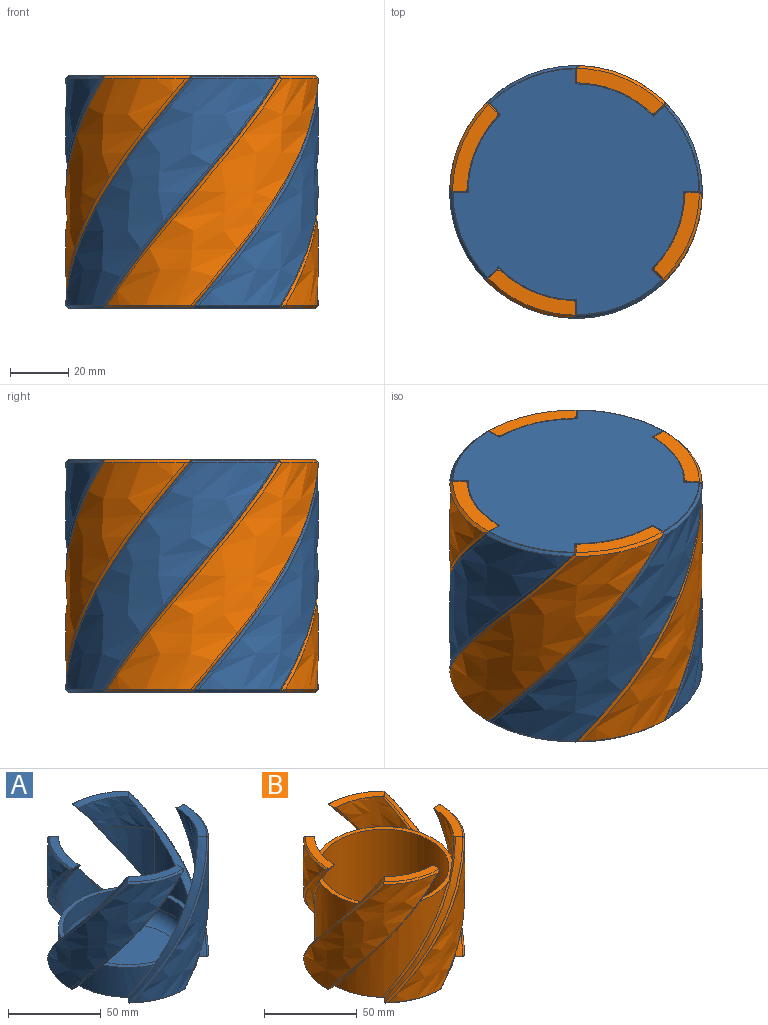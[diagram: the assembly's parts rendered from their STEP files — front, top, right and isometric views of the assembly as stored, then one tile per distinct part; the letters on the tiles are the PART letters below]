
ASSEMBLY  parts=2 mates=1
PART A: 76 faces, bbox 90.4x90.4x84.8 mm
  f0: cylinder r=35mm len=70mm, axis (0,0,-1), area 2199.1mm2, adj f10,f75
  f1: plane 55x55mm, normal (0,0,1), area 2375.8mm2, adj f75
  f2: extruded ~40x21.23mm, area 633.3mm2, adj f9,f10,f35,f62
  f3: extruded ~40x20.3mm, area 589.1mm2, adj f6,f29,f34
  f4: extruded ~40x21.23mm, area 636.5mm2, adj f7,f10,f30,f60
  f5: extruded ~51.58x28.32mm, area 652mm2, adj f8,f10,f22,f26,f61
  f6: cylinder r=37.5mm len=40mm, axis (0,0,1), area 589mm2, adj f3,f10,f31
  f7: cylinder r=37.5mm len=40mm, axis (0,0,1), area 589mm2, adj f4,f10,f27
  f8: cylinder r=37.5mm len=40mm, axis (0,0,1), area 589mm2, adj f5,f10,f23
  f9: cylinder r=37.5mm len=40mm, axis (0,0,1), area 589mm2, adj f2,f10,f20
  f10: plane 75.28x75.28mm, normal (0,0,1), area 570.6mm2, adj f0,f2,f4,f5,f6,f7,f8,f9
  f11: plane 31.88x16.3mm, normal (0,0,1), area 157.3mm2, adj f20,f33,f35,f43,f62
  f12: bspline ~80x74.26mm, area 2456.9mm2, adj f36,f43,f73,f74
  f13: plane 30.37x16.3mm, normal (0,0,1), area 157.1mm2, adj f29,f31,f34,f42
  f14: bspline ~80x74.26mm, area 2456.9mm2, adj f39,f42,f67,f68
  f15: bspline ~80x74.26mm, area 2456.9mm2, adj f38,f40,f69,f70
  f16: plane 31.88x16.3mm, normal (0,0,1), area 157.5mm2, adj f25,f27,f30,f40,f60
  f17: bspline ~80x74.26mm, area 2456.9mm2, adj f37,f41,f71,f72
  f18: plane 84.89x84.89mm, normal (0,0,-1), area 4975.6mm2, adj f44,f45,f46,f47,f48,f49,f50,f51
  f19: plane 30.86x16.3mm, normal (0,0,1), area 155.4mm2, adj f22,f23,f26,f41
  f20: bspline ~80x61.52mm, area 480.8mm2, adj f9,f10,f11,f35,f51,f65,f74
  f21: cylinder r=37.5mm len=32.72mm, axis (0,0,-1), area 533mm2, adj f10,f49,f51,f61,f65
  f22: bspline ~80x43.5mm, area 424.4mm2, adj f5,f19,f26,f47,f49,f61,f72
  f23: bspline ~80x61.52mm, area 480.8mm2, adj f8,f10,f19,f26,f44,f64,f71
  f24: cylinder r=37.5mm len=32.72mm, axis (0,0,-1), area 533mm2, adj f10,f44,f46,f60,f64
  f25: bspline ~80x43.5mm, area 409.3mm2, adj f16,f46,f48,f60,f70
  f26: bspline ~37.09x27.91mm, area 589.1mm2, adj f5,f19,f22,f23
  f27: bspline ~80x61.52mm, area 480.8mm2, adj f7,f10,f16,f30,f52,f63,f69
  f28: cylinder r=37.5mm len=33.94mm, axis (0,0,-1), area 557mm2, adj f10,f29,f52,f54,f63
  f29: bspline ~80x43.5mm, area 507.3mm2, adj f3,f13,f28,f34,f54,f56,f67
  f30: bspline ~37.42x27.95mm, area 609.4mm2, adj f4,f16,f27,f60
  f31: bspline ~80x61.52mm, area 480.8mm2, adj f6,f10,f13,f34,f59,f66,f68
  f32: cylinder r=37.5mm len=32.72mm, axis (0,0,-1), area 533mm2, adj f10,f57,f59,f62,f66
  f33: bspline ~80x43.5mm, area 409.3mm2, adj f11,f55,f57,f62,f73
  f34: bspline ~36.22x27.79mm, area 589.1mm2, adj f3,f13,f29,f31
  f35: bspline ~37.42x27.95mm, area 609.4mm2, adj f2,f11,f20,f62
  f36: bspline ~34.56x14.63mm, area 42.7mm2, adj f12,f51,f53,f55,f73,f74
  f37: bspline ~34.56x14.63mm, area 42.7mm2, adj f17,f44,f45,f47,f71,f72
  f38: bspline ~34.56x14.63mm, area 42.7mm2, adj f15,f48,f50,f52,f69,f70
  f39: bspline ~34.56x14.63mm, area 42.7mm2, adj f14,f56,f58,f59,f67,f68
  f40: bspline ~33.18x14.18mm, area 45.9mm2, adj f15,f16,f69,f70
  f41: bspline ~33.18x14.18mm, area 45.9mm2, adj f17,f19,f71,f72
  f42: bspline ~33.18x14.18mm, area 45.9mm2, adj f13,f14,f67,f68
  f43: bspline ~33.18x14.18mm, area 45.9mm2, adj f11,f12,f73,f74
  f44: bspline ~5.08x4.97mm, area 3.1mm2, adj f18,f23,f24,f37,f45,f46,f64,f71
  f45: bspline ~33.07x13.86mm, area 7.5mm2, adj f18,f37,f44,f47
  f46: cone r=37.5mm half-angle=45deg, axis (0,0,1), area 13mm2, adj f18,f24,f25,f44,f48,f60
  f47: bspline ~5.41x0.24mm, area 1.4mm2, adj f18,f22,f37,f45,f49,f72
  f48: bspline ~5.41x0.24mm, area 1.4mm2, adj f18,f25,f38,f46,f50,f70
  f49: cone r=37.5mm half-angle=45deg, axis (0,0,1), area 13mm2, adj f18,f21,f22,f47,f51,f61
  f50: bspline ~33.07x13.86mm, area 7.5mm2, adj f18,f38,f48,f52
  f51: bspline ~5.08x4.97mm, area 3.1mm2, adj f18,f20,f21,f36,f49,f53,f65,f74
  f52: bspline ~5.08x4.97mm, area 3.1mm2, adj f18,f27,f28,f38,f50,f54,f63,f69
  f53: bspline ~33.07x13.86mm, area 7.5mm2, adj f18,f36,f51,f55
  f54: cone r=37.5mm half-angle=45deg, axis (0,0,1), area 12.6mm2, adj f18,f28,f29,f52,f56
  f55: bspline ~5.41x0.24mm, area 1.4mm2, adj f18,f33,f36,f53,f57,f73
  f56: bspline ~5.41x0.24mm, area 1.4mm2, adj f18,f29,f39,f54,f58,f67
  f57: cone r=37.5mm half-angle=45deg, axis (0,0,1), area 13mm2, adj f18,f32,f33,f55,f59,f62
  f58: bspline ~33.07x13.86mm, area 7.5mm2, adj f18,f39,f56,f59
  f59: bspline ~5.08x4.97mm, area 3.1mm2, adj f18,f31,f32,f39,f57,f58,f66,f68
  f60: bspline ~83.97x40.91mm, area 148.1mm2, adj f4,f10,f16,f24,f25,f30,f46
  f61: bspline ~76.86x39.2mm, area 122.8mm2, adj f5,f10,f21,f22,f49
  f62: bspline ~83.97x40.91mm, area 147.8mm2, adj f2,f10,f11,f32,f33,f35,f57
  f63: bspline ~22.31x13.88mm, area 36.8mm2, adj f10,f27,f28,f52
  f64: bspline ~22.31x13.88mm, area 36.8mm2, adj f10,f23,f24,f44
  f65: bspline ~22.31x13.88mm, area 36.8mm2, adj f10,f20,f21,f51
  f66: bspline ~22.31x13.88mm, area 36.8mm2, adj f10,f31,f32,f59
  f67: bspline ~82.98x45.29mm, area 162.9mm2, adj f14,f29,f39,f42,f56
  f68: bspline ~81.23x62.41mm, area 163.2mm2, adj f14,f31,f39,f42,f59
  f69: bspline ~81.23x62.41mm, area 163.2mm2, adj f15,f27,f38,f40,f52
  f70: bspline ~82.98x45.29mm, area 162.9mm2, adj f15,f25,f38,f40,f48
  f71: bspline ~81.23x62.41mm, area 163.2mm2, adj f17,f23,f37,f41,f44
  f72: bspline ~82.98x45.29mm, area 162.9mm2, adj f17,f22,f37,f41,f47
  f73: bspline ~82.98x45.29mm, area 162.9mm2, adj f12,f33,f36,f43,f55
  f74: bspline ~81.23x62.41mm, area 163.2mm2, adj f12,f20,f36,f43,f51
  f75: torus R=27.5mm, axis (0,0,1), area 2389mm2, adj f0,f1
PART B: 76 faces, bbox 90.4x90.4x84.3 mm
  f0: cylinder r=37.5mm len=59.7mm, axis (0,0,-1), area 1613.4mm2, adj f4,f41,f43,f70,f75
  f1: cylinder r=37.5mm len=59.7mm, axis (0,0,-1), area 1613.4mm2, adj f4,f36,f38,f69,f74
  f2: cylinder r=37.5mm len=59.7mm, axis (0,0,-1), area 1613.4mm2, adj f4,f44,f46,f72,f73
  f3: cylinder r=37.5mm len=59.7mm, axis (0,0,-1), area 1685.4mm2, adj f4,f16,f49,f51,f71
  f4: plane 75.28x75.28mm, normal (0,0,1), area 573.4mm2, adj f0,f1,f2,f3,f6,f8,f13,f16
  f5: plane 84.89x84.89mm, normal (0,0,-1), area 4975.6mm2, adj f36,f37,f38,f39,f40,f41,f42,f43
  f6: cylinder r=35mm len=70mm, axis (0,0,-1), area 10995.6mm2, adj f4,f68
  f7: plane 55x55mm, normal (0,0,1), area 2375.8mm2, adj f68
  f8: bspline ~36.22x27.79mm, area 540.2mm2, adj f4,f9,f66,f67
  f9: plane 30.37x15.85mm, normal (0,0,1), area 156.6mm2, adj f8,f10,f11,f33,f66,f67
  f10: bspline ~80x43.5mm, area 409.2mm2, adj f9,f47,f49,f52,f66,f71
  f11: bspline ~80x61.52mm, area 406.5mm2, adj f9,f43,f53,f67,f75
  f12: bspline ~80x74.26mm, area 2456.9mm2, adj f31,f33,f52,f53
  f13: bspline ~36.22x27.79mm, area 540.2mm2, adj f4,f14,f64,f65
  f14: plane 30.37x15.85mm, normal (0,0,1), area 156.6mm2, adj f13,f15,f16,f32,f64,f65
  f15: bspline ~80x43.5mm, area 409.2mm2, adj f14,f46,f48,f58,f64,f72
  f16: bspline ~80x61.52mm, area 480.2mm2, adj f3,f4,f14,f51,f59,f65
  f17: bspline ~80x74.26mm, area 2456.9mm2, adj f28,f32,f58,f59
  f18: bspline ~36.22x27.79mm, area 540.2mm2, adj f4,f19,f62,f63
  f19: plane 30.37x15.85mm, normal (0,0,1), area 156.7mm2, adj f18,f21,f22,f35,f62,f63
  f20: bspline ~80x74.26mm, area 2456.9mm2, adj f29,f35,f56,f57
  f21: bspline ~80x43.5mm, area 409.2mm2, adj f19,f38,f40,f57,f62,f69
  f22: bspline ~80x61.52mm, area 406.5mm2, adj f19,f44,f56,f63,f73
  f23: bspline ~36.22x27.79mm, area 540.2mm2, adj f4,f24,f60,f61
  f24: plane 30.37x15.85mm, normal (0,0,1), area 155mm2, adj f23,f26,f27,f34,f60,f61
  f25: bspline ~80x74.26mm, area 2456.9mm2, adj f30,f34,f54,f55
  f26: bspline ~80x43.5mm, area 409.2mm2, adj f24,f39,f41,f55,f60,f70
  f27: bspline ~80x61.52mm, area 406.5mm2, adj f24,f36,f54,f61,f74
  f28: bspline ~34.56x14.63mm, area 42.7mm2, adj f17,f48,f50,f51,f58,f59
  f29: bspline ~34.56x14.63mm, area 42.7mm2, adj f20,f40,f42,f44,f56,f57
  f30: bspline ~34.56x14.63mm, area 42.7mm2, adj f25,f36,f37,f39,f54,f55
  f31: bspline ~34.56x14.63mm, area 42.7mm2, adj f12,f43,f45,f47,f52,f53
  f32: bspline ~33.18x14.18mm, area 45.9mm2, adj f14,f17,f58,f59
  f33: bspline ~33.18x14.18mm, area 45.9mm2, adj f9,f12,f52,f53
  f34: bspline ~33.18x14.18mm, area 45.9mm2, adj f24,f25,f54,f55
  f35: bspline ~33.18x14.18mm, area 45.9mm2, adj f19,f20,f56,f57
  f36: bspline ~5.08x4.97mm, area 3.1mm2, adj f1,f5,f27,f30,f37,f38,f54,f74
  f37: bspline ~33.07x13.86mm, area 7.5mm2, adj f5,f30,f36,f39
  f38: cone r=37.5mm half-angle=45deg, axis (0,0,1), area 13mm2, adj f1,f5,f21,f36,f40,f69
  f39: bspline ~5.41x0.24mm, area 1.4mm2, adj f5,f26,f30,f37,f41,f55
  f40: bspline ~5.41x0.24mm, area 1.4mm2, adj f5,f21,f29,f38,f42,f57
  f41: cone r=37.5mm half-angle=45deg, axis (0,0,1), area 13mm2, adj f0,f5,f26,f39,f43,f70
  f42: bspline ~33.07x13.86mm, area 7.5mm2, adj f5,f29,f40,f44
  f43: bspline ~5.08x4.97mm, area 3.1mm2, adj f0,f5,f11,f31,f41,f45,f53,f75
  f44: bspline ~5.08x4.97mm, area 3.1mm2, adj f2,f5,f22,f29,f42,f46,f56,f73
  f45: bspline ~33.07x13.86mm, area 7.5mm2, adj f5,f31,f43,f47
  f46: cone r=37.5mm half-angle=45deg, axis (0,0,1), area 13mm2, adj f2,f5,f15,f44,f48,f72
  f47: bspline ~5.41x0.24mm, area 1.4mm2, adj f5,f10,f31,f45,f49,f52
  f48: bspline ~5.41x0.24mm, area 1.4mm2, adj f5,f15,f28,f46,f50,f58
  f49: cone r=37.5mm half-angle=45deg, axis (0,0,1), area 13mm2, adj f3,f5,f10,f47,f51,f71
  f50: bspline ~33.07x13.86mm, area 7.5mm2, adj f5,f28,f48,f51
  f51: bspline ~4.72x4.63mm, area 2.9mm2, adj f3,f5,f16,f28,f49,f50,f59
  f52: bspline ~82.98x45.29mm, area 162.9mm2, adj f10,f12,f31,f33,f47
  f53: bspline ~81.23x62.41mm, area 163.2mm2, adj f11,f12,f31,f33,f43
  f54: bspline ~81.23x62.41mm, area 163.2mm2, adj f25,f27,f30,f34,f36
  f55: bspline ~82.98x45.29mm, area 162.9mm2, adj f25,f26,f30,f34,f39
  f56: bspline ~81.23x62.41mm, area 163.2mm2, adj f20,f22,f29,f35,f44
  f57: bspline ~82.98x45.29mm, area 162.9mm2, adj f20,f21,f29,f35,f40
  f58: bspline ~82.98x45.29mm, area 162.9mm2, adj f15,f17,f28,f32,f48
  f59: bspline ~81.23x62.41mm, area 163.2mm2, adj f16,f17,f28,f32,f51
  f60: bspline ~24.9x18.07mm, area 38.7mm2, adj f4,f23,f24,f26
  f61: bspline ~26.01x16.48mm, area 38.7mm2, adj f4,f23,f24,f27
  f62: bspline ~24.9x18.07mm, area 38.7mm2, adj f4,f18,f19,f21
  f63: bspline ~26.01x16.48mm, area 38.7mm2, adj f4,f18,f19,f22
  f64: bspline ~24.9x18.07mm, area 38.7mm2, adj f4,f13,f14,f15
  f65: bspline ~26.01x16.48mm, area 38.7mm2, adj f4,f13,f14,f16
  f66: bspline ~24.9x18.07mm, area 38.7mm2, adj f4,f8,f9,f10
  f67: bspline ~26.01x16.48mm, area 38.7mm2, adj f4,f8,f9,f11
  f68: torus R=27.5mm, axis (0,0,1), area 2389mm2, adj f6,f7
  f69: bspline ~64.21x36.86mm, area 114.6mm2, adj f1,f4,f21,f38
  f70: bspline ~64.21x36.86mm, area 114.6mm2, adj f0,f4,f26,f41
  f71: bspline ~64.21x36.86mm, area 114.6mm2, adj f3,f4,f10,f49
  f72: bspline ~64.21x36.86mm, area 114.6mm2, adj f2,f4,f15,f46
  f73: bspline ~63.89x44.12mm, area 114.3mm2, adj f2,f4,f22,f44
  f74: bspline ~63.89x44.12mm, area 114.3mm2, adj f1,f4,f27,f36
  f75: bspline ~63.89x44.12mm, area 114.3mm2, adj f0,f4,f11,f43
PLACE A rot(axis=(0,1,0),180deg) t=(-16.31,89.13,77.82)mm
PLACE B t=(-16.31,-10.87,-2.18)mm fixed
MATE cylindrical A.f0 <-> B.f0  axis (0,0,-1) through (-16.31,-10.87,57.82)mm
